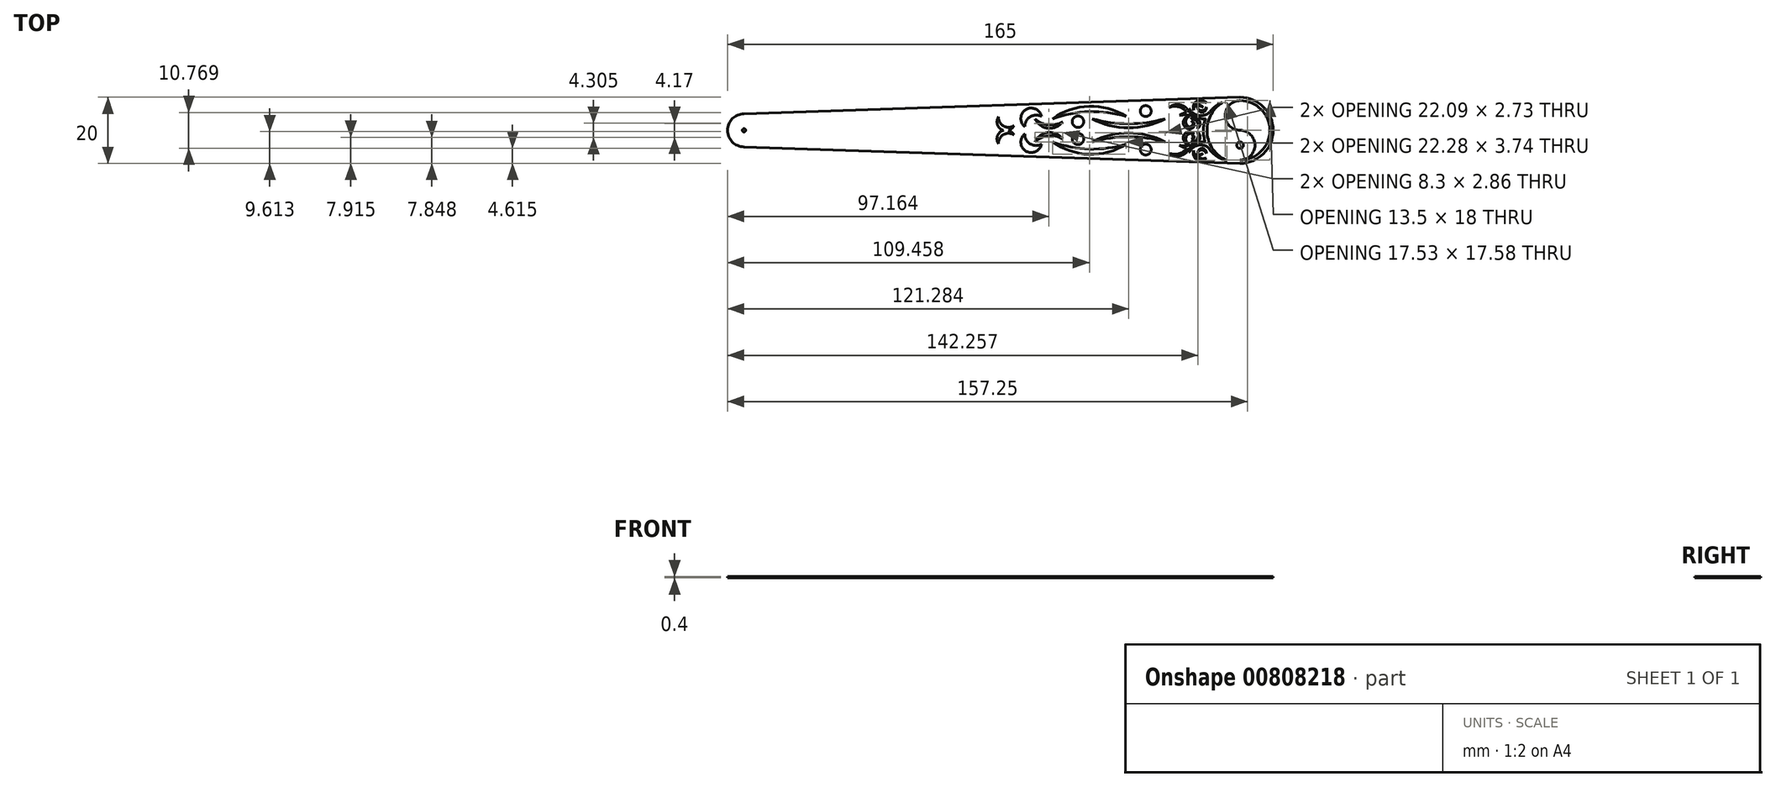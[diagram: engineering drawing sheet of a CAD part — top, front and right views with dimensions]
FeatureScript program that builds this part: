
annotation { "Feature Type Name" : "Feature", "Feature Type Description" : "" }
export const myFeature = defineFeature(function(context is Context, id is Id, definition is map)
    precondition{}
    {
        {
            var Q0;
            Q0=qCreatedBy(makeId("Top.planeOp"),FACE);
            var sketch = newSketch(context, id + "F0", { "sketchPlane" : qUnion([Q0])});
            skCircle(sketch, "E0", {"center": v(0, 0) * mm, "radius": 5 * mm});
            skLineSegment(sketch, "E1", {"start": v(0, 0) * mm, "end": v(150, 0) * mm, "construction": true});
            skLineSegment(sketch, "E2", {"start": v(150, 0) * mm, "end": v(150, -10) * mm, "construction": true});
            skLineSegment(sketch, "E3", {"start": v(150, 0) * mm, "end": v(150, 10) * mm, "construction": true});
            skLineSegment(sketch, "E4", {"start": v(0, 5) * mm, "end": v(150, 10) * mm});
            skLineSegment(sketch, "E5", {"start": v(0, -5) * mm, "end": v(150, -10) * mm});
            skArc(sketch, "E6", {"start": v(150, -10) * mm, "mid": v(160.34, 0) * mm, "end": v(150, 10) * mm});
            skCircle(sketch, "E7", {"center": v(150, 0) * mm, "radius": 9 * mm});
            skArc(sketch, "E8", {"start": v(150, 9) * mm, "mid": v(145.5, 4.5) * mm, "end": v(150, 0) * mm});
            skArc(sketch, "E9", {"start": v(149.37, -8.96) * mm, "mid": v(154.49, -4.82) * mm, "end": v(150, 0) * mm});
            skCircle(sketch, "E10", {"center": v(150, -4.5) * mm, "radius": 1 * mm});
            skCircle(sketch, "E11", {"center": v(0, 0) * mm, "radius": 0.5 * mm});
            skCircle(sketch, "E12.0", {"center": v(150, 0) * mm, "radius": 10 * mm});
            skArc(sketch, "E13", {"start": v(144.58, 8.4) * mm, "mid": v(138.9, -0.91) * mm, "end": v(146.02, -9.17) * mm});
            skArc(sketch, "E14", {"start": v(134.65, 6.64) * mm, "mid": v(137.79, 4.45) * mm, "end": v(141.26, 6.06) * mm});
            skArc(sketch, "E15", {"start": v(134.65, 6.64) * mm, "mid": v(136.55, 4.14) * mm, "end": v(139.64, 3.55) * mm});
            skArc(sketch, "E16", {"start": v(136.55, 4.14) * mm, "mid": v(134.14, 4.63) * mm, "end": v(131.67, 4.56) * mm});
            skArc(sketch, "E17", {"start": v(135.32, 5.27) * mm, "mid": v(133.42, 5.28) * mm, "end": v(131.67, 4.56) * mm});
            skArc(sketch, "E18", {"start": v(137.27, 6.54) * mm, "mid": v(138.74, 5.47) * mm, "end": v(139.75, 6.98) * mm});
            skArc(sketch, "E19", {"start": v(139.75, 8.39) * mm, "mid": v(136.9, 8.83) * mm, "end": v(135.95, 6.1) * mm});
            skArc(sketch, "E20", {"start": v(139.75, 8.39) * mm, "mid": v(137.29, 8.17) * mm, "end": v(135.95, 6.1) * mm});
            skArc(sketch, "E21", {"start": v(137.1, 0.5) * mm, "mid": v(137.64, 3.05) * mm, "end": v(135.07, 3.52) * mm});
            skArc(sketch, "E22", {"start": v(137.27, 6.54) * mm, "mid": v(138.65, 5.99) * mm, "end": v(139.75, 6.98) * mm});
            skArc(sketch, "E23", {"start": v(138.74, 6.98) * mm, "mid": v(137.76, 7.57) * mm, "end": v(136.78, 6.98) * mm});
            skArc(sketch, "E24", {"start": v(138.74, 6.98) * mm, "mid": v(137.76, 7.33) * mm, "end": v(136.78, 6.98) * mm});
            skArc(sketch, "E25", {"start": v(137.1, 0.5) * mm, "mid": v(137, 2.62) * mm, "end": v(135.07, 3.52) * mm});
            skArc(sketch, "E26", {"start": v(134.65, 4.2) * mm, "mid": v(133.76, 1.88) * mm, "end": v(136.13, 1.12) * mm});
            skArc(sketch, "E27", {"start": v(134.65, 4.2) * mm, "mid": v(132.98, 1.5) * mm, "end": v(136.13, 1.12) * mm});
            skArc(sketch, "E28", {"start": v(135.29, 1.47) * mm, "mid": v(136.13, 2.03) * mm, "end": v(135.3, 2.62) * mm});
            skArc(sketch, "E29", {"start": v(135.29, 1.47) * mm, "mid": v(135.8, 2.04) * mm, "end": v(135.3, 2.62) * mm});
            skArc(sketch, "E30", {"start": v(134.65, 5.36) * mm, "mid": v(131.95, 7.67) * mm, "end": v(128.5, 6.9) * mm});
            skArc(sketch, "E31", {"start": v(133.88, 5.35) * mm, "mid": v(131.47, 7.1) * mm, "end": v(128.5, 6.9) * mm});
            skArc(sketch, "E32", {"start": v(105.24, 3.52) * mm, "mid": v(116.28, 0.79) * mm, "end": v(127.33, 3.52) * mm});
            skArc(sketch, "E33", {"start": v(105.24, 3.52) * mm, "mid": v(116.28, 1.97) * mm, "end": v(127.33, 3.52) * mm});
            skArc(sketch, "E34", {"start": v(115.6, 4.2) * mm, "mid": v(104.35, 7.25) * mm, "end": v(93.32, 3.52) * mm});
            skArc(sketch, "E35", {"start": v(115.6, 4.2) * mm, "mid": v(104.4, 5.65) * mm, "end": v(93.32, 3.52) * mm});
            skArc(sketch, "E36", {"start": v(88.01, 3.52) * mm, "mid": v(92.01, 1.65) * mm, "end": v(96.31, 2.62) * mm});
            skArc(sketch, "E37", {"start": v(88.01, 3.52) * mm, "mid": v(91.9, 0.65) * mm, "end": v(96.31, 2.62) * mm});
            skArc(sketch, "E38", {"start": v(89.95, 4.2) * mm, "mid": v(85.22, 6.28) * mm, "end": v(84.9, 1.12) * mm});
            skArc(sketch, "E39", {"start": v(89.95, 4.2) * mm, "mid": v(86.54, 4.11) * mm, "end": v(84.9, 1.12) * mm});
            skCircle(sketch, "E40", {"center": v(101, 2.62) * mm, "radius": 1.73 * mm});
            skArc(sketch, "E41", {"start": v(76.9, 4.05) * mm, "mid": v(77.84, 0.25) * mm, "end": v(81.59, 1.36) * mm});
            skArc(sketch, "E42", {"start": v(76.9, 4.05) * mm, "mid": v(78.45, 1.31) * mm, "end": v(81.59, 1.36) * mm});
            skArc(sketch, "E43.MirrorCS", {"start": v(76.9, -4.05) * mm, "mid": v(78.45, -1.31) * mm, "end": v(81.59, -1.36) * mm});
            skArc(sketch, "E44.MirrorCS", {"start": v(76.9, -4.05) * mm, "mid": v(77.84, -0.25) * mm, "end": v(81.59, -1.36) * mm});
            skArc(sketch, "E45.MirrorCS", {"start": v(89.95, -4.2) * mm, "mid": v(85.22, -6.28) * mm, "end": v(84.9, -1.12) * mm});
            skArc(sketch, "E46.MirrorCS", {"start": v(89.95, -4.2) * mm, "mid": v(86.54, -4.11) * mm, "end": v(84.9, -1.12) * mm});
            skArc(sketch, "E47.MirrorCS", {"start": v(88.01, -3.52) * mm, "mid": v(91.9, -0.65) * mm, "end": v(96.31, -2.62) * mm});
            skArc(sketch, "E48.MirrorCS", {"start": v(88.01, -3.52) * mm, "mid": v(92.01, -1.65) * mm, "end": v(96.31, -2.62) * mm});
            skArc(sketch, "E49.MirrorCS", {"start": v(115.6, -4.2) * mm, "mid": v(104.35, -7.25) * mm, "end": v(93.32, -3.52) * mm});
            skCircle(sketch, "E50.MirrorC", {"center": v(101, -2.62) * mm, "radius": 1.73 * mm});
            skArc(sketch, "E51.MirrorCS", {"start": v(115.6, -4.2) * mm, "mid": v(104.4, -5.65) * mm, "end": v(93.32, -3.52) * mm});
            skArc(sketch, "E52.MirrorCS", {"start": v(105.24, -3.52) * mm, "mid": v(116.28, -1.97) * mm, "end": v(127.33, -3.52) * mm});
            skArc(sketch, "E53.MirrorCS", {"start": v(105.24, -3.52) * mm, "mid": v(116.28, -0.79) * mm, "end": v(127.33, -3.52) * mm});
            skArc(sketch, "E54.MirrorCS", {"start": v(133.88, -5.35) * mm, "mid": v(131.47, -7.1) * mm, "end": v(128.5, -6.9) * mm});
            skArc(sketch, "E55.MirrorCS", {"start": v(134.65, -5.36) * mm, "mid": v(131.95, -7.67) * mm, "end": v(128.5, -6.9) * mm});
            skArc(sketch, "E56.MirrorCS", {"start": v(136.55, -4.14) * mm, "mid": v(134.14, -4.63) * mm, "end": v(131.67, -4.56) * mm});
            skArc(sketch, "E57.MirrorCS", {"start": v(135.32, -5.27) * mm, "mid": v(133.42, -5.28) * mm, "end": v(131.67, -4.56) * mm});
            skArc(sketch, "E58.MirrorCS", {"start": v(134.65, -6.64) * mm, "mid": v(136.55, -4.14) * mm, "end": v(139.64, -3.55) * mm});
            skArc(sketch, "E59.MirrorCS", {"start": v(134.65, -6.64) * mm, "mid": v(137.79, -4.45) * mm, "end": v(141.26, -6.06) * mm});
            skArc(sketch, "E60.MirrorCS", {"start": v(137.1, -0.5) * mm, "mid": v(137.64, -3.05) * mm, "end": v(135.07, -3.52) * mm});
            skArc(sketch, "E61.MirrorCS", {"start": v(137.1, -0.5) * mm, "mid": v(137, -2.62) * mm, "end": v(135.07, -3.52) * mm});
            skArc(sketch, "E62.MirrorCS", {"start": v(134.65, -4.2) * mm, "mid": v(133.76, -1.88) * mm, "end": v(136.13, -1.12) * mm});
            skArc(sketch, "E63.MirrorCS", {"start": v(134.65, -4.2) * mm, "mid": v(132.98, -1.5) * mm, "end": v(136.13, -1.12) * mm});
            skArc(sketch, "E64.MirrorCS", {"start": v(138.74, -6.98) * mm, "mid": v(137.76, -7.33) * mm, "end": v(136.78, -6.98) * mm});
            skArc(sketch, "E65.MirrorCS", {"start": v(138.74, -6.98) * mm, "mid": v(137.76, -7.57) * mm, "end": v(136.78, -6.98) * mm});
            skArc(sketch, "E66.MirrorCS", {"start": v(139.75, -8.39) * mm, "mid": v(137.29, -8.17) * mm, "end": v(135.95, -6.1) * mm});
            skArc(sketch, "E67.MirrorCS", {"start": v(139.75, -8.39) * mm, "mid": v(136.9, -8.83) * mm, "end": v(135.95, -6.1) * mm});
            skArc(sketch, "E68.MirrorCS", {"start": v(137.27, -6.54) * mm, "mid": v(138.74, -5.47) * mm, "end": v(139.75, -6.98) * mm});
            skArc(sketch, "E69.MirrorCS", {"start": v(137.27, -6.54) * mm, "mid": v(138.65, -5.99) * mm, "end": v(139.75, -6.98) * mm});
            skArc(sketch, "E70.MirrorCS", {"start": v(135.29, -1.47) * mm, "mid": v(136.13, -2.03) * mm, "end": v(135.3, -2.62) * mm});
            skArc(sketch, "E71.MirrorCS", {"start": v(135.29, -1.47) * mm, "mid": v(135.8, -2.04) * mm, "end": v(135.3, -2.62) * mm});
            skCircle(sketch, "E72", {"center": v(121.46, 5.82) * mm, "radius": 1.66 * mm});
            skCircle(sketch, "E73.MirrorC", {"center": v(121.46, -5.82) * mm, "radius": 1.66 * mm});
            skSolve(sketch);
        }
        {
            var Q0;
            {var subQ1=sQuery(id+"F0.wireOp",EDGE,"E4");Q0=makeQuery(id+"F0.imprint","IMPRINT",FACE,{"disambiguationData":[TD([[makeQuery(id+"F0.imprint","IMPRINT",EDGE,{"derivedFrom":subQ1}),-1.0]])]});}
            var Q1;
            {var subQ0=sQuery(id+"F0.wireOp",EDGE,"E0");var subQ3=makeQuery(id+"F0.imprint","IMPRINT",VERTEX,{"derivedFrom":subQ0});Q1=makeQuery(id+"F0.imprint","IMPRINT",FACE,{"disambiguationData":[TD([[makeQuery(id+"F0.imprint","IMPRINT",EDGE,{"disambiguationData":[TD([[subQ3,1.0]])],"derivedFrom":subQ0}),1.0]])]});}
            var Q2;
            {var subQ0=sQuery(id+"F0.wireOp",EDGE,"E8");Q2=makeQuery(id+"F0.imprint","IMPRINT",FACE,{"disambiguationData":[TD([[makeQuery(id+"F0.imprint","IMPRINT",EDGE,{"derivedFrom":subQ0}),-1.0]])]});}
            var Q3;
            Q3=makeQuery(id+"F0.imprint","IMPRINT",FACE,{"disambiguationData":[TD([[makeQuery(id+"F0.imprint","IMPRINT",EDGE,{"derivedFrom":sQuery(id+"F0.wireOp",EDGE,"E11")}),-1.0]])]});
            var Q4;
            {var subQ31=sQuery(id+"F0.wireOp",EDGE,"E16");Q4=makeQuery(id+"F0.imprint","IMPRINT",FACE,{"disambiguationData":[TD([[makeQuery(id+"F0.imprint","IMPRINT",EDGE,{"derivedFrom":subQ31}),1.0]])]});}
            extrude(context, id + "F1", {"entities" : qUnion([Q0, Q1, Q2, Q3, Q4]), "depth" : 0.4 * mm, "offsetDistance" : 25 * mm});
        }
    });
